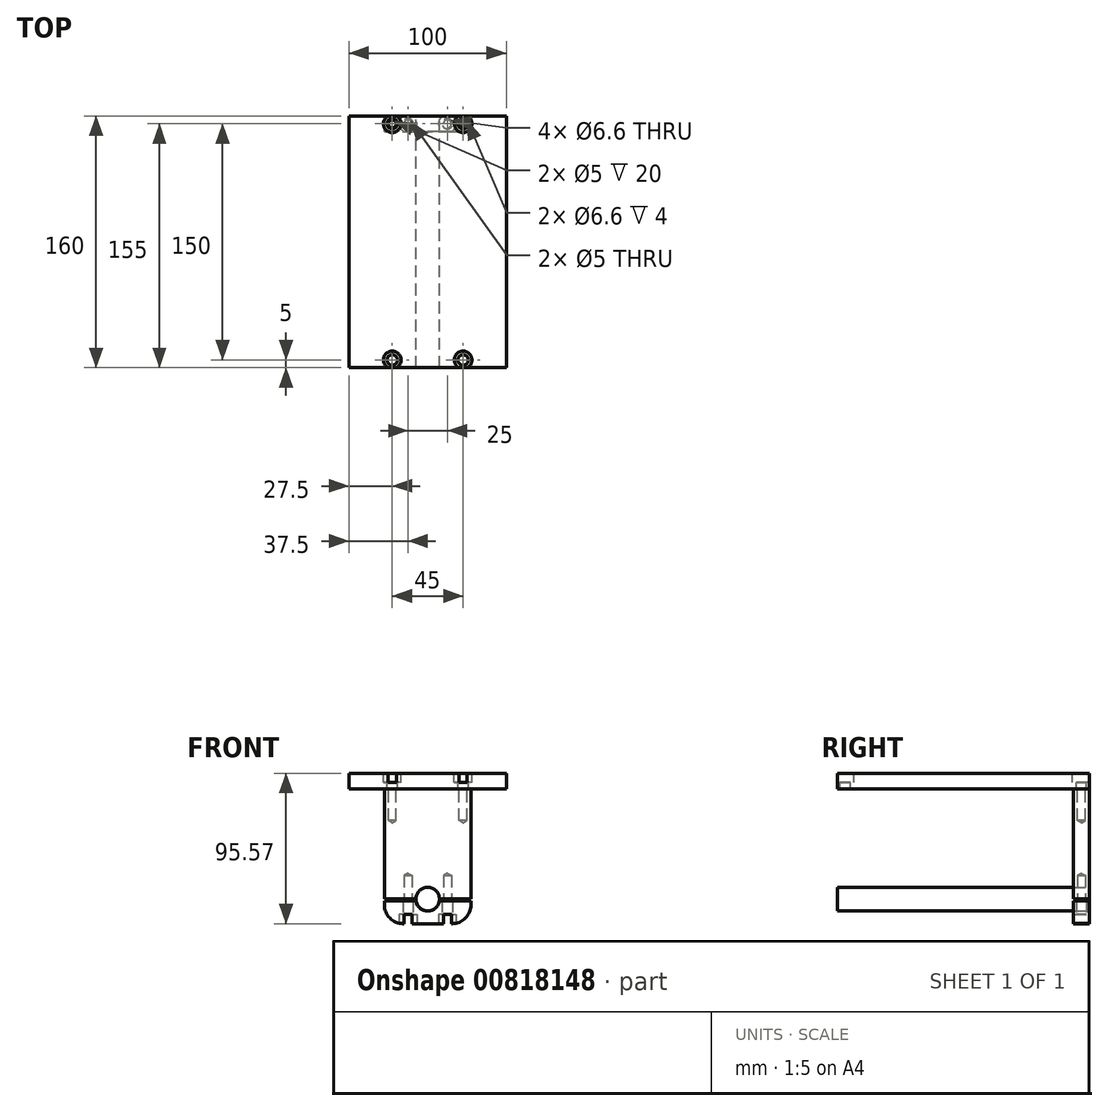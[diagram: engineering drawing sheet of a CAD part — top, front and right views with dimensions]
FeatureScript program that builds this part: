
annotation { "Feature Type Name" : "Feature", "Feature Type Description" : "" }
export const myFeature = defineFeature(function(context is Context, id is Id, definition is map)
    precondition{}
    {
        {
            var Q0;
            Q0=qCreatedBy(makeId("Front.planeOp"),FACE);
            var sketch = newSketch(context, id + "F0", { "sketchPlane" : qUnion([Q0])});
            skLineSegment(sketch, "E0.top", {"start": v(-27.5, 70) * mm, "end": v(27.5, 70) * mm});
            skLineSegment(sketch, "E0.left", {"start": v(-27.5, 0) * mm, "end": v(-27.5, 70) * mm});
            skLineSegment(sketch, "E0.right", {"start": v(27.5, 0) * mm, "end": v(27.5, 70) * mm});
            skPoint(sketch, "E1", {"position": v(0, 70) * mm});
            skLineSegment(sketch, "E2", {"start": v(27.5, 0) * mm, "end": v(7.5, 0) * mm});
            skLineSegment(sketch, "E3", {"start": v(-27.5, 0) * mm, "end": v(-7.5, 0) * mm});
            skPoint(sketch, "E4.visualSharp", {"position": v(-27.5, 0) * mm});
            skPoint(sketch, "E5.visualSharp", {"position": v(27.5, 0) * mm});
            skArc(sketch, "E6", {"start": v(7.5, 0) * mm, "mid": v(0, 7.5) * mm, "end": v(-7.5, 0) * mm});
            skLineSegment(sketch, "E7.bottom", {"start": v(27.5, -1) * mm, "end": v(7.5, -1) * mm});
            skLineSegment(sketch, "E7.top", {"start": v(15.5, -15.57) * mm, "end": v(-15.5, -15.57) * mm});
            skLineSegment(sketch, "E7.left", {"start": v(27.5, -1) * mm, "end": v(27.5, -3.57) * mm});
            skLineSegment(sketch, "E7.right", {"start": v(-27.5, -1) * mm, "end": v(-27.5, -3.57) * mm});
            skArc(sketch, "E8", {"start": v(7.5, -1) * mm, "mid": v(0, -7.57) * mm, "end": v(-7.5, -1) * mm});
            skLineSegment(sketch, "E9.trimOffspring", {"start": v(-7.5, -1) * mm, "end": v(-27.5, -1) * mm});
            skPoint(sketch, "E10.visualSharp", {"position": v(27.5, -15.57) * mm});
            skArc(sketch, "E10.filletArc", {"start": v(15.5, -15.57) * mm, "mid": v(23.99, -12.05) * mm, "end": v(27.5, -3.57) * mm});
            skPoint(sketch, "E11.visualSharp", {"position": v(-27.5, -15.57) * mm});
            skArc(sketch, "E11.filletArc", {"start": v(-27.5, -3.57) * mm, "mid": v(-23.99, -12.05) * mm, "end": v(-15.5, -15.57) * mm});
            skSolve(sketch);
        }
        {
            var Q0;
            Q0=makeQuery(id+"F0.imprint","IMPRINT",FACE,{"disambiguationData":[TD([[makeQuery(id+"F0.imprint","IMPRINT",EDGE,{"derivedFrom":sQuery(id+"F0.wireOp",EDGE,"E0.top")}),-1.0]])]});
            var Q1;
            Q1=makeQuery(id+"F0.imprint","IMPRINT",FACE,{"disambiguationData":[TD([[makeQuery(id+"F0.imprint","IMPRINT",EDGE,{"derivedFrom":sQuery(id+"F0.wireOp",EDGE,"E7.bottom")}),1.0]])]});
            extrude(context, id + "F1", {"entities" : qUnion([Q0, Q1]), "depth" : 10 * mm, "offsetDistance" : 25 * mm});
        }
        {
            var Q0;
            Q0=makeQuery(id+"F1.opExtrude","SWEPT_FACE",FACE,{"disambiguationData":[OSD([sQuery(id+"F0.wireOp",EDGE,"E0.top")])]});
            var sketch = newSketch(context, id + "F2", { "sketchPlane" : qUnion([Q0])});
            skPoint(sketch, "E12.centerSnap0", {"position": v(-27.5, -5) * mm});
            skPoint(sketch, "E13.centerSnap0", {"position": v(27.5, -5) * mm});
            skPoint(sketch, "E14", {"position": v(-22.5, -5) * mm});
            skPoint(sketch, "E15", {"position": v(22.5, -5) * mm});
            skSolve(sketch);
        }
        {
            var Q0;
            Q0=sQuery(id+"F2.wireOp",VERTEX,"E14");
            var Q1;
            Q1=sQuery(id+"F2.wireOp",VERTEX,"E15");
            var Q2;
            Q2=makeQuery(id+"F1.opExtrude","SWEPT_BODY",BODY,{"disambiguationData":[OSD([sQuery(id+"F0.wireOp",EDGE,"04XgqUot-V3Du-IATu-pYUY-Fnh2cVdjSxI2"),sQuery(id+"F0.wireOp",EDGE,"E0.top"),sQuery(id+"F0.wireOp",EDGE,"E0.left"),sQuery(id+"F0.wireOp",EDGE,"E0.right"),sQuery(id+"F0.wireOp",EDGE,"fe7d51b6-e1a8-4b0c-ab00-6fe90d1e24ea"),sQuery(id+"F0.wireOp",EDGE,"51sOFWCz-F9EK-aYgv-ijSG-XZlUBzvnZtY1"),sQuery(id+"F0.wireOp",EDGE,"ntcde3FJ-BVGZ-e07j-rwW4-g3WMyRL1kpFk"),sQuery(id+"F0.wireOp",EDGE,"82fc1eed-c275-4081-b3be-bd8e519b5def.trimOffspring")])]});
            hole(context, id + "F3", {"style" : HoleStyle.SIMPLE, "endStyle" : HoleEndStyle.BLIND, "standardTappedOrClearance" : lookupTablePath({ "standard" : "ISO", "engagement" : "75%", "pitch" : "1 mm", "size" : "M6", "type" : "Tapped" }), "standardBlindInLast" : lookupTablePath({ "standard" : "ISO", "engagement" : "75%", "pitch" : "1 mm", "size" : "M6", "type" : "Tapped" }), "holeDiameter" : 5 * mm, "majorDiameter" : 6 * mm, "showTappedDepth" : true, "holeDepth" : 20 * mm, "tappedDepth" : 17 * mm, "tapClearance" : 3, "locations" : qUnion([Q0, Q1]), "scope" : qUnion([Q2])});
        }
        {
            var Q0;
            Q0=makeQuery(id+"F1.opExtrude","SWEPT_FACE",FACE,{"disambiguationData":[OSD([sQuery(id+"F0.wireOp",EDGE,"E0.top")])]});
            var sketch = newSketch(context, id + "F4", { "sketchPlane" : qUnion([Q0])});
            skLineSegment(sketch, "E16.bottom", {"start": v(-50, 0) * mm, "end": v(50, 0) * mm});
            skLineSegment(sketch, "E16.top", {"start": v(-50, -80) * mm, "end": v(50, -80) * mm});
            skLineSegment(sketch, "E16.left", {"start": v(-50, -80) * mm, "end": v(-50, 0) * mm});
            skLineSegment(sketch, "E16.right", {"start": v(50, -80) * mm, "end": v(50, 0) * mm});
            skPoint(sketch, "E17", {"position": v(0, 0) * mm});
            skSolve(sketch);
        }
        {
            var Q0;
            Q0=makeQuery(id+"F4.imprint","IMPRINT",FACE,{"disambiguationData":[TD([[makeQuery(id+"F4.imprint","IMPRINT",EDGE,{"derivedFrom":sQuery(id+"F4.wireOp",EDGE,"E16.top")}),1.0]])]});
            var Q1;
            {var subQ0=sQuery(id+"F0.wireOp",EDGE,"E0.top");Q1=makeQuery(id+"F4.imprint","IMPRINT",FACE,{"disambiguationData":[TD([[makeQuery(id+"F4.imprint","IMPRINT",EDGE,{"derivedFrom":makeQuery(id+"F1.opExtrude","CAP_EDGE",EDGE,{"disambiguationData":[OSD([subQ0])],"isStart":false})}),1.0]])]});}
            extrude(context, id + "F5", {"entities" : qUnion([Q0, Q1]), "depth" : 10 * mm, "offsetDistance" : 25 * mm});
        }
        {
            var Q0;
            Q0=makeQuery(id+"F5.opExtrude","CAP_FACE",FACE,{"disambiguationData":[OSD([sQuery(id+"F3.hole-0.sketch.wireOp",EDGE,"core_line_2"),sQuery(id+"F3.hole-0.sketch.wireOp",EDGE,"core_line_3"),sQuery(id+"F3.hole-1.sketch.wireOp",EDGE,"core_line_2"),sQuery(id+"F3.hole-1.sketch.wireOp",EDGE,"core_line_3"),sQuery(id+"F4.wireOp",EDGE,"E16.bottom"),sQuery(id+"F4.wireOp",EDGE,"E16.top"),sQuery(id+"F4.wireOp",EDGE,"E16.left"),sQuery(id+"F4.wireOp",EDGE,"E16.right")])],"isStart":false});
            var sketch = newSketch(context, id + "F6", { "sketchPlane" : qUnion([Q0])});
            skPoint(sketch, "E18", {"position": v(-22.5, -5) * mm});
            skPoint(sketch, "E19", {"position": v(22.5, -5) * mm});
            skSolve(sketch);
        }
        {
            var Q0;
            Q0=sQuery(id+"F6.wireOp",VERTEX,"E18");
            var Q1;
            Q1=sQuery(id+"F6.wireOp",VERTEX,"E19");
            var Q2;
            Q2=makeQuery(id+"F5.opExtrude","SWEPT_BODY",BODY,{"disambiguationData":[OSD([sQuery(id+"F3.hole-0.sketch.wireOp",EDGE,"core_line_2"),sQuery(id+"F3.hole-0.sketch.wireOp",EDGE,"core_line_3"),sQuery(id+"F3.hole-1.sketch.wireOp",EDGE,"core_line_2"),sQuery(id+"F3.hole-1.sketch.wireOp",EDGE,"core_line_3"),sQuery(id+"F4.wireOp",EDGE,"E16.bottom"),sQuery(id+"F4.wireOp",EDGE,"E16.top"),sQuery(id+"F4.wireOp",EDGE,"E16.left"),sQuery(id+"F4.wireOp",EDGE,"E16.right")])]});
            hole(context, id + "F7", {"style" : HoleStyle.C_BORE, "endStyle" : HoleEndStyle.BLIND, "standardTappedOrClearance" : lookupTablePath({ "standard" : "ISO", "fit" : "Normal", "size" : "M6", "type" : "Clearance" }), "standardBlindInLast" : lookupTablePath({ "fit" : "Standard", "standard" : "ISO", "size" : "M6", "type" : "Clearance" }), "holeDiameter" : 6.6 * mm, "cBoreDiameter" : 11.25 * mm, "cBoreDepth" : 6 * mm, "majorDiameter" : 5 * mm, "holeDepth" : 20 * mm, "tappedDepth" : 17 * mm, "tapClearance" : 3, "locations" : qUnion([Q0, Q1]), "scope" : qUnion([Q2])});
        }
        {
            var Q0;
            Q0=makeQuery(id+"F5.opExtrude","SWEPT_BODY",BODY,{"disambiguationData":[OSD([sQuery(id+"F3.hole-0.sketch.wireOp",EDGE,"core_line_2"),sQuery(id+"F3.hole-0.sketch.wireOp",EDGE,"core_line_3"),sQuery(id+"F3.hole-1.sketch.wireOp",EDGE,"core_line_2"),sQuery(id+"F3.hole-1.sketch.wireOp",EDGE,"core_line_3"),sQuery(id+"F4.wireOp",EDGE,"E16.bottom"),sQuery(id+"F4.wireOp",EDGE,"E16.top"),sQuery(id+"F4.wireOp",EDGE,"E16.left"),sQuery(id+"F4.wireOp",EDGE,"E16.right")])]});
            var Q1;
            Q1=makeQuery(id+"F5.opExtrude","SWEPT_FACE",FACE,{"disambiguationData":[OSD([sQuery(id+"F4.wireOp",EDGE,"E16.top")])]});
            mirror(context, id + "F8", {"operationType" : NewBodyOperationType.ADD, "entities" : qUnion([Q0]), "mirrorPlane" : qUnion([Q1])});
        }
        {
            var Q0;
            Q0=makeQuery(id+"F1.opExtrude","SWEPT_FACE",FACE,{"disambiguationData":[OSD([sQuery(id+"F0.wireOp",EDGE,"E3")])]});
            var sketch = newSketch(context, id + "F9", { "sketchPlane" : qUnion([Q0])});
            skPoint(sketch, "E20", {"position": v(-12.5, 5) * mm});
            skPoint(sketch, "E20.positionSnap0", {"position": v(-7.5, 5) * mm});
            skPoint(sketch, "E21", {"position": v(12.5, 5) * mm});
            skSolve(sketch);
        }
        {
            var Q0;
            Q0=sQuery(id+"F9.wireOp",VERTEX,"E20");
            var Q1;
            Q1=sQuery(id+"F9.wireOp",VERTEX,"E21");
            var Q2;
            Q2=makeQuery(id+"F1.opExtrude","SWEPT_BODY",BODY,{"disambiguationData":[OSD([sQuery(id+"F0.wireOp",EDGE,"E0.top"),sQuery(id+"F0.wireOp",EDGE,"E0.left"),sQuery(id+"F0.wireOp",EDGE,"E0.right"),sQuery(id+"F0.wireOp",EDGE,"E2"),sQuery(id+"F0.wireOp",EDGE,"E3"),sQuery(id+"F0.wireOp",EDGE,"E6")])]});
            hole(context, id + "F10", {"style" : HoleStyle.SIMPLE, "endStyle" : HoleEndStyle.BLIND, "standardTappedOrClearance" : lookupTablePath({ "standard" : "ISO", "engagement" : "75%", "pitch" : "1 mm", "size" : "M6", "type" : "Tapped" }), "standardBlindInLast" : lookupTablePath({ "standard" : "ISO", "engagement" : "75%", "pitch" : "1 mm", "size" : "M6", "type" : "Tapped" }), "holeDiameter" : 5 * mm, "majorDiameter" : 6 * mm, "showTappedDepth" : true, "holeDepth" : 15 * mm, "tappedDepth" : 12 * mm, "tapClearance" : 3, "startFromSketch" : true, "locations" : qUnion([Q0, Q1]), "scope" : qUnion([Q2])});
        }
        {
            var Q0;
            Q0=makeQuery(id+"F1.opExtrude","SWEPT_FACE",FACE,{"disambiguationData":[OSD([sQuery(id+"F0.wireOp",EDGE,"E7.top")])]});
            var sketch = newSketch(context, id + "F11", { "sketchPlane" : qUnion([Q0])});
            skPoint(sketch, "E22", {"position": v(-12.5, 5) * mm});
            skPoint(sketch, "E23", {"position": v(12.5, 5) * mm});
            skSolve(sketch);
        }
        {
            var Q0;
            Q0=sQuery(id+"F11.wireOp",VERTEX,"E22");
            var Q1;
            Q1=sQuery(id+"F11.wireOp",VERTEX,"E23");
            var Q2;
            Q2=makeQuery(id+"F1.opExtrude","SWEPT_BODY",BODY,{"disambiguationData":[OSD([sQuery(id+"F0.wireOp",EDGE,"E7.bottom"),sQuery(id+"F0.wireOp",EDGE,"E7.top"),sQuery(id+"F0.wireOp",EDGE,"E7.left"),sQuery(id+"F0.wireOp",EDGE,"E7.right"),sQuery(id+"F0.wireOp",EDGE,"E8"),sQuery(id+"F0.wireOp",EDGE,"E9.trimOffspring"),sQuery(id+"F0.wireOp",EDGE,"E10.filletArc"),sQuery(id+"F0.wireOp",EDGE,"E11.filletArc")])]});
            hole(context, id + "F12", {"style" : HoleStyle.C_BORE, "endStyle" : HoleEndStyle.BLIND, "standardTappedOrClearance" : lookupTablePath({ "standard" : "ISO", "fit" : "Normal", "size" : "M6", "type" : "Clearance" }), "standardBlindInLast" : lookupTablePath({ "fit" : "Standard", "standard" : "ISO", "size" : "M6", "type" : "Clearance" }), "holeDiameter" : 6.6 * mm, "cBoreDiameter" : 11.25 * mm, "cBoreDepth" : 6 * mm, "majorDiameter" : 5 * mm, "holeDepth" : 20 * mm, "tappedDepth" : 17 * mm, "tapClearance" : 3, "startFromSketch" : true, "locations" : qUnion([Q0, Q1]), "scope" : qUnion([Q2])});
        }
        {
            var Q0;
            Q0=makeQuery(id+"F1.opExtrude","CAP_FACE",FACE,{"disambiguationData":[OSD([sQuery(id+"F0.wireOp",EDGE,"E0.top"),sQuery(id+"F0.wireOp",EDGE,"E0.left"),sQuery(id+"F0.wireOp",EDGE,"E0.right"),sQuery(id+"F0.wireOp",EDGE,"E2"),sQuery(id+"F0.wireOp",EDGE,"E3"),sQuery(id+"F0.wireOp",EDGE,"E6")])],"isStart":true});
            var sketch = newSketch(context, id + "F13", { "sketchPlane" : qUnion([Q0])});
            skCircle(sketch, "E24", {"center": v(0, 0) * mm, "radius": 7.5 * mm});
            skSolve(sketch);
        }
        {
            var Q0;
            {var subQ0=sQuery(id+"F13.wireOp",EDGE,"E24");Q0=makeQuery(id+"F13.imprint","IMPRINT",FACE,{"disambiguationData":[TD([[makeQuery(id+"F13.imprint","IMPRINT",EDGE,{"disambiguationData":[OD(0.0)],"derivedFrom":subQ0}),-1.0]])]});}
            var Q1;
            Q1=makeQuery(id+"F8.opPattern","COPY",FACE,{"derivedFrom":makeQuery(id+"F5.opExtrude","SWEPT_FACE",FACE,{"disambiguationData":[OSD([sQuery(id+"F4.wireOp",EDGE,"E16.bottom")])]}),"instanceName":"1"});
            extrude(context, id + "F14", {"entities" : qUnion([Q0]), "endBound" : BoundingType.UP_TO_SURFACE, "oppositeDirection" : true, "depth" : 25 * mm, "endBoundEntityFace" : qUnion([Q1]), "offsetDistance" : 25 * mm});
        }
    });
